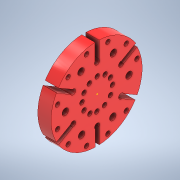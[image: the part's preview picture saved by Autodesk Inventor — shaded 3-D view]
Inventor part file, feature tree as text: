
AUTODESK INVENTOR PART (.ipt)
format: ipt  version: 2021 (Build 250183000, 183)  size: 267,776 bytes
history: native  units: in
note: dims shown in document units (in); Inventor stores cm internally (conversion verified against a paired STEP export)
features: sketch x2, extrude x1
ambient origin geometry x8: Origin, YZ Plane, XZ Plane, XY Plane, X Axis, Y Axis, Z Axis, Center Point
bodies: Solid1 (feature_tree)
feature tree (3):
  sketch  "Sketch2"  dims[d1=0.0689in d2=0.1969in]
  extrude  "Extrusion1"  Depth=0.0689in
  sketch  "Sketch9"  dims[d8=0.1181in d9=0.9055in d11=1.2598in d13=0.1575in d16=2.3622in d18=360.0deg d23=1.6535in d24=2.3622in d26=360.0deg d28=2.6772in d29=0.3937in d30=0.0in]
